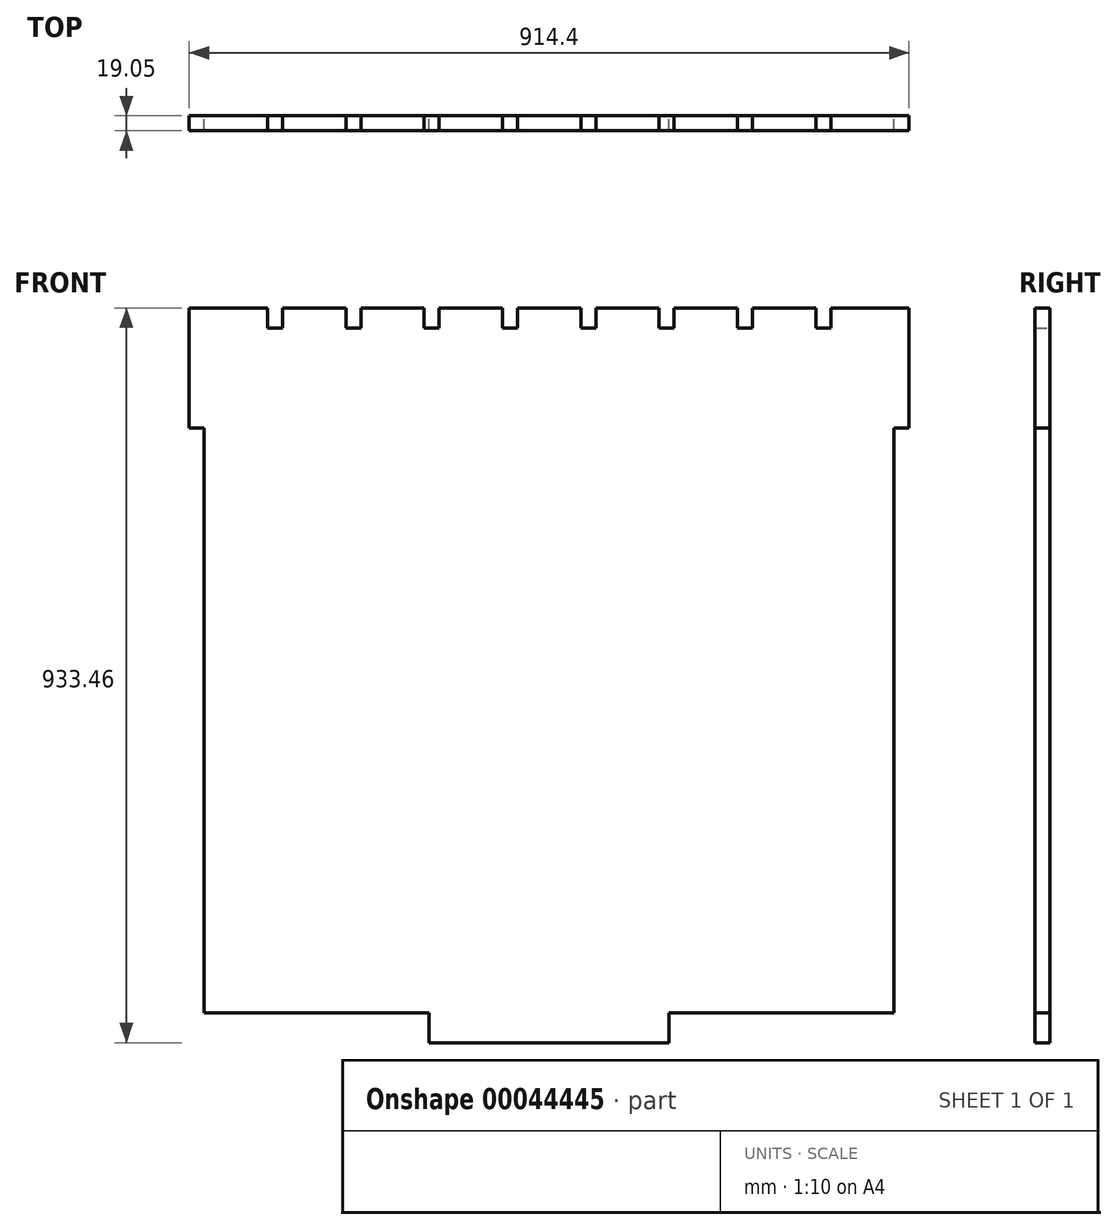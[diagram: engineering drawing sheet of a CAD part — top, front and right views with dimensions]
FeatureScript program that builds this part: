
annotation { "Feature Type Name" : "Feature", "Feature Type Description" : "" }
export const myFeature = defineFeature(function(context is Context, id is Id, definition is map)
    precondition{}
    {
        {
            var Q0;
            Q0=qCreatedBy(makeId("Front.planeOp"),FACE);
            var sketch = newSketch(context, id + "F0", { "sketchPlane" : qUnion([Q0])});
            skLineSegment(sketch, "E0.rect.bottom", {"start": v(-438.15, 447.68) * mm, "end": v(438.15, 447.68) * mm});
            skLineSegment(sketch, "E0.rect.top", {"start": v(-438.15, -447.68) * mm, "end": v(438.15, -447.68) * mm});
            skLineSegment(sketch, "E0.rect.left", {"start": v(-438.15, 447.68) * mm, "end": v(-438.15, -447.68) * mm});
            skLineSegment(sketch, "E0.rect.right", {"start": v(438.15, 447.68) * mm, "end": v(438.15, -447.68) * mm});
            skPoint(sketch, "E0.rect.middle", {"position": v(0, 0) * mm});
            skLineSegment(sketch, "E1.bottom", {"start": v(-438.15, 447.68) * mm, "end": v(-457.2, 447.68) * mm});
            skLineSegment(sketch, "E1.top", {"start": v(-438.15, 295.28) * mm, "end": v(-457.2, 295.28) * mm});
            skLineSegment(sketch, "E1.left", {"start": v(-438.15, 447.68) * mm, "end": v(-438.15, 295.28) * mm});
            skLineSegment(sketch, "E1.right", {"start": v(-457.2, 447.68) * mm, "end": v(-457.2, 295.28) * mm});
            skLineSegment(sketch, "E2.bottom", {"start": v(-152.4, -447.68) * mm, "end": v(152.4, -447.68) * mm});
            skLineSegment(sketch, "E2.top", {"start": v(-152.4, -485.78) * mm, "end": v(152.4, -485.78) * mm});
            skLineSegment(sketch, "E2.left", {"start": v(-152.4, -447.68) * mm, "end": v(-152.4, -485.78) * mm});
            skLineSegment(sketch, "E2.right", {"start": v(152.4, -447.68) * mm, "end": v(152.4, -485.78) * mm});
            skLineSegment(sketch, "E3.MirrorCS", {"start": v(438.15, 447.68) * mm, "end": v(457.2, 447.68) * mm});
            skLineSegment(sketch, "E4.MirrorCS", {"start": v(438.15, 295.27) * mm, "end": v(457.2, 295.27) * mm});
            skLineSegment(sketch, "E5.MirrorCS", {"start": v(438.15, 447.68) * mm, "end": v(-438.15, 447.68) * mm});
            skLineSegment(sketch, "E6.MirrorCS", {"start": v(438.15, -447.68) * mm, "end": v(-438.15, -447.68) * mm});
            skLineSegment(sketch, "E7.MirrorCS", {"start": v(152.4, -485.78) * mm, "end": v(-152.4, -485.78) * mm});
            skLineSegment(sketch, "E8.MirrorCS", {"start": v(152.4, -447.68) * mm, "end": v(-152.4, -447.68) * mm});
            skLineSegment(sketch, "E9.MirrorCS", {"start": v(438.15, 447.68) * mm, "end": v(438.15, 295.28) * mm});
            skLineSegment(sketch, "E10.MirrorCS", {"start": v(457.2, 447.68) * mm, "end": v(457.2, 295.28) * mm});
            skLineSegment(sketch, "E11.bottom", {"start": v(-357.72, 447.68) * mm, "end": v(-338.67, 447.68) * mm});
            skLineSegment(sketch, "E11.top", {"start": v(-357.72, 422.28) * mm, "end": v(-338.67, 422.28) * mm});
            skLineSegment(sketch, "E11.left", {"start": v(-357.72, 447.68) * mm, "end": v(-357.72, 422.28) * mm});
            skLineSegment(sketch, "E11.right", {"start": v(-338.67, 447.68) * mm, "end": v(-338.67, 422.28) * mm});
            skLineSegment(sketch, "E12.bottom", {"start": v(-258.23, 447.68) * mm, "end": v(-239.18, 447.68) * mm});
            skLineSegment(sketch, "E12.top", {"start": v(-258.23, 422.28) * mm, "end": v(-239.18, 422.28) * mm});
            skLineSegment(sketch, "E12.left", {"start": v(-258.23, 447.68) * mm, "end": v(-258.23, 422.28) * mm});
            skLineSegment(sketch, "E12.right", {"start": v(-239.18, 447.68) * mm, "end": v(-239.18, 422.28) * mm});
            skLineSegment(sketch, "E13.bottom", {"start": v(-158.75, 447.68) * mm, "end": v(-139.7, 447.68) * mm});
            skLineSegment(sketch, "E13.top", {"start": v(-158.75, 422.28) * mm, "end": v(-139.7, 422.28) * mm});
            skLineSegment(sketch, "E13.left", {"start": v(-158.75, 447.68) * mm, "end": v(-158.75, 422.28) * mm});
            skLineSegment(sketch, "E13.right", {"start": v(-139.7, 447.68) * mm, "end": v(-139.7, 422.28) * mm});
            skLineSegment(sketch, "E14.left", {"start": v(139.7, 447.68) * mm, "end": v(139.7, 422.28) * mm});
            skLineSegment(sketch, "E15.right", {"start": v(59.27, 447.68) * mm, "end": v(59.27, 422.28) * mm});
            skLineSegment(sketch, "E16.right", {"start": v(-40.22, 447.68) * mm, "end": v(-40.22, 422.28) * mm});
            skLineSegment(sketch, "E16.left", {"start": v(-59.27, 447.68) * mm, "end": v(-59.27, 422.28) * mm});
            skLineSegment(sketch, "E14.right", {"start": v(158.75, 447.68) * mm, "end": v(158.75, 422.28) * mm});
            skLineSegment(sketch, "E15.left", {"start": v(40.22, 447.68) * mm, "end": v(40.22, 422.28) * mm});
            skLineSegment(sketch, "E16.top", {"start": v(-59.27, 422.28) * mm, "end": v(-40.22, 422.28) * mm});
            skLineSegment(sketch, "E15.top", {"start": v(40.22, 422.28) * mm, "end": v(59.27, 422.28) * mm});
            skLineSegment(sketch, "E14.top", {"start": v(139.7, 422.28) * mm, "end": v(158.75, 422.28) * mm});
            skLineSegment(sketch, "E16.bottom", {"start": v(-59.27, 447.68) * mm, "end": v(-40.22, 447.68) * mm});
            skLineSegment(sketch, "E15.bottom", {"start": v(40.22, 447.68) * mm, "end": v(59.27, 447.68) * mm});
            skLineSegment(sketch, "E14.bottom", {"start": v(139.7, 447.68) * mm, "end": v(158.75, 447.68) * mm});
            skLineSegment(sketch, "E17.bottom", {"start": v(239.18, 447.68) * mm, "end": v(258.23, 447.68) * mm});
            skLineSegment(sketch, "E17.top", {"start": v(239.18, 422.28) * mm, "end": v(258.23, 422.28) * mm});
            skLineSegment(sketch, "E17.left", {"start": v(239.18, 447.68) * mm, "end": v(239.18, 422.28) * mm});
            skLineSegment(sketch, "E17.right", {"start": v(258.23, 447.68) * mm, "end": v(258.23, 422.28) * mm});
            skLineSegment(sketch, "E18.bottom", {"start": v(338.67, 447.68) * mm, "end": v(357.72, 447.68) * mm});
            skLineSegment(sketch, "E18.top", {"start": v(338.67, 422.28) * mm, "end": v(357.72, 422.28) * mm});
            skLineSegment(sketch, "E18.left", {"start": v(338.67, 447.68) * mm, "end": v(338.67, 422.28) * mm});
            skLineSegment(sketch, "E18.right", {"start": v(357.72, 447.68) * mm, "end": v(357.72, 422.28) * mm});
            skSolve(sketch);
        }
        {
            var Q0;
            {var subQ4=sQuery(id+"F0.wireOp",EDGE,"E0.rect.left");Q0=makeQuery(id+"F0.imprint","IMPRINT",FACE,{"disambiguationData":[TD([[makeQuery(id+"F0.imprint","IMPRINT",EDGE,{"derivedFrom":subQ4}),1.0]])]});}
            var Q1;
            Q1=makeQuery(id+"F0.imprint","IMPRINT",FACE,{"disambiguationData":[TD([[makeQuery(id+"F0.imprint","IMPRINT",EDGE,{"derivedFrom":sQuery(id+"F0.wireOp",EDGE,"E1.bottom")}),1.0]])]});
            var Q2;
            Q2=makeQuery(id+"F0.imprint","IMPRINT",FACE,{"disambiguationData":[TD([[makeQuery(id+"F0.imprint","IMPRINT",EDGE,{"derivedFrom":sQuery(id+"F0.wireOp",EDGE,"E2.top")}),1.0]])]});
            var Q3;
            Q3=makeQuery(id+"F0.imprint","IMPRINT",FACE,{"disambiguationData":[TD([[makeQuery(id+"F0.imprint","IMPRINT",EDGE,{"derivedFrom":sQuery(id+"F0.wireOp",EDGE,"E2.left")}),1.0]])]});
            var Q4;
            Q4=makeQuery(id+"F0.imprint","IMPRINT",FACE,{"disambiguationData":[TD([[makeQuery(id+"F0.imprint","IMPRINT",EDGE,{"derivedFrom":sQuery(id+"F0.wireOp",EDGE,"E3.MirrorCS")}),-1.0]])]});
            extrude(context, id + "F1", {"entities" : qUnion([Q0, Q1, Q2, Q3, Q4]), "depth" : 19.05 * mm});
        }
    });
